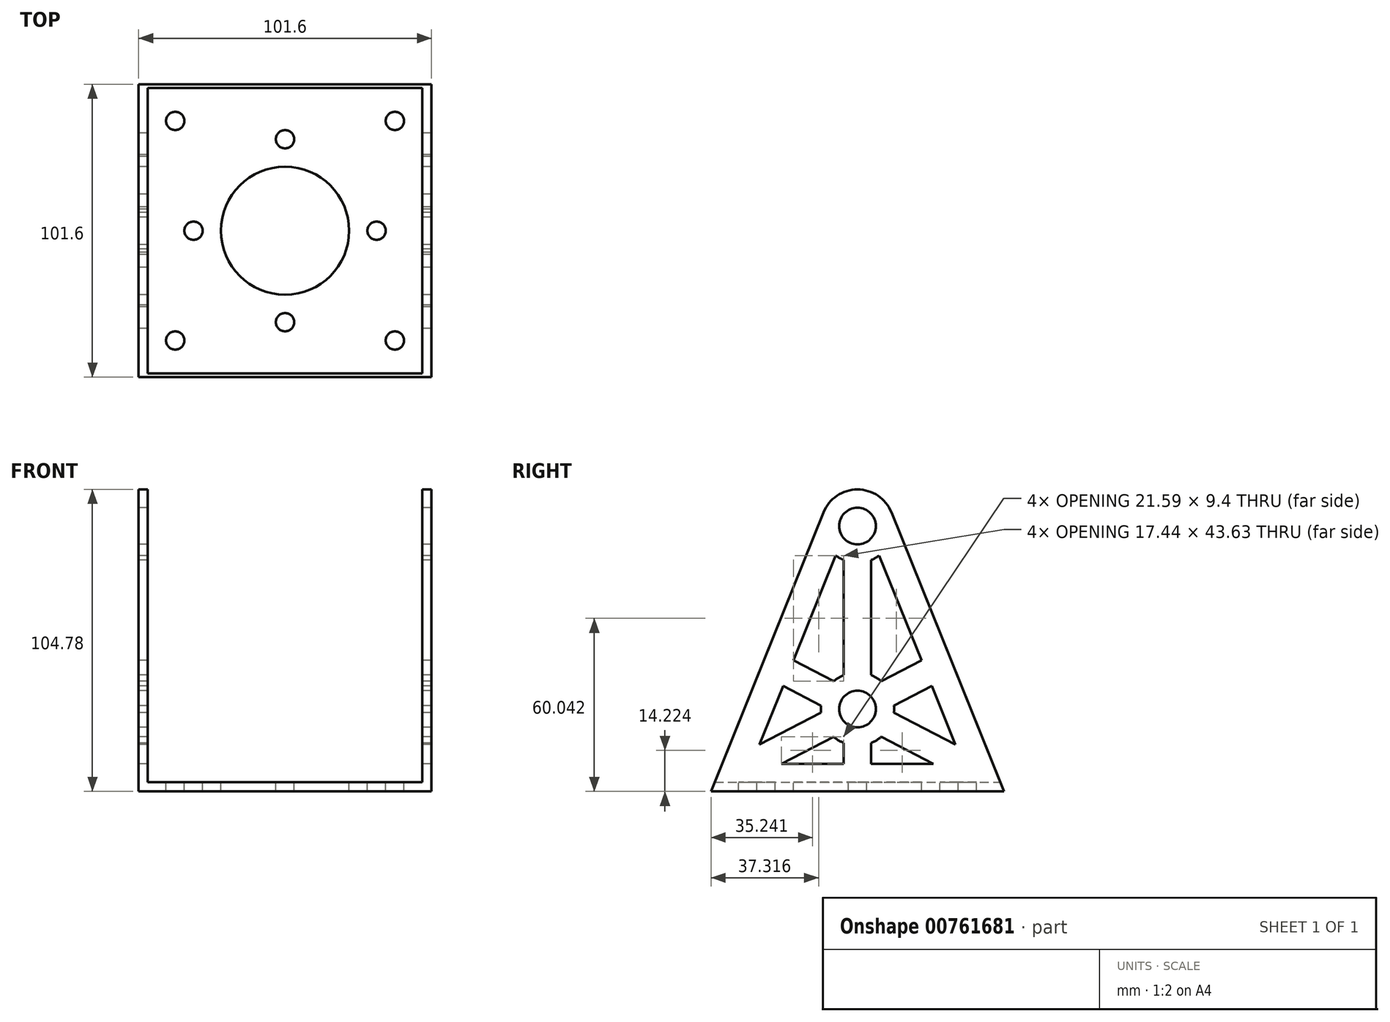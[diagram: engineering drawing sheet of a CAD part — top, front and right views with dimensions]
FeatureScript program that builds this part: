
annotation { "Feature Type Name" : "Feature", "Feature Type Description" : "" }
export const myFeature = defineFeature(function(context is Context, id is Id, definition is map)
    precondition{}
    {
        {
            var Q0;
            Q0=qCreatedBy(makeId("Top.planeOp"),FACE);
            var sketch = newSketch(context, id + "F0", { "sketchPlane" : qUnion([Q0])});
            skLineSegment(sketch, "E0.bottom", {"start": v(50.8, 50.8) * mm, "end": v(-50.8, 50.8) * mm});
            skLineSegment(sketch, "E0.top", {"start": v(50.8, -50.8) * mm, "end": v(-50.8, -50.8) * mm});
            skLineSegment(sketch, "E0.left", {"start": v(50.8, 50.8) * mm, "end": v(50.8, -50.8) * mm});
            skLineSegment(sketch, "E0.right", {"start": v(-50.8, 50.8) * mm, "end": v(-50.8, -50.8) * mm});
            skPoint(sketch, "E0.middle", {"position": v(0, 0) * mm});
            skSolve(sketch);
        }
        {
            var Q0;
            Q0 = qSketchRegion(id + "F0", true);
            extrude(context, id + "F1", {"entities" : qUnion([Q0]), "depth" : 3.17 * mm, "offsetDistance" : 25.4 * mm});
        }
        {
            var Q0;
            Q0=makeQuery(id+"F1.opExtrude","CAP_FACE",FACE,{"disambiguationData":[OSD([sQuery(id+"F0.wireOp",EDGE,"E0.bottom"),sQuery(id+"F0.wireOp",EDGE,"E0.top"),sQuery(id+"F0.wireOp",EDGE,"E0.left"),sQuery(id+"F0.wireOp",EDGE,"E0.right")])],"isStart":false});
            var sketch = newSketch(context, id + "F2", { "sketchPlane" : qUnion([Q0])});
            skLineSegment(sketch, "E1", {"start": v(-50.8, 50.8) * mm, "end": v(-50.8, -50.8) * mm});
            skLineSegment(sketch, "E2", {"start": v(-50.8, -50.8) * mm, "end": v(-47.62, -50.8) * mm});
            skLineSegment(sketch, "E3", {"start": v(-47.62, -50.8) * mm, "end": v(-47.63, 50.8) * mm});
            skLineSegment(sketch, "E4", {"start": v(-47.63, 50.8) * mm, "end": v(-50.8, 50.8) * mm});
            skSolve(sketch);
        }
        {
            var Q0;
            Q0=makeQuery(id+"F2.imprint","IMPRINT",FACE,{"disambiguationData":[TD([[makeQuery(id+"F2.imprint","IMPRINT",EDGE,{"derivedFrom":sQuery(id+"F2.wireOp",EDGE,"E1")}),1.0]])]});
            extrude(context, id + "F3", {"entities" : qUnion([Q0]), "operationType" : NewBodyOperationType.ADD, "depth" : 101.6 * mm, "offsetDistance" : 25.4 * mm});
        }
        {
            var Q0;
            Q0=makeQuery(id+"F1.opExtrude","CAP_FACE",FACE,{"disambiguationData":[OSD([sQuery(id+"F0.wireOp",EDGE,"E0.bottom"),sQuery(id+"F0.wireOp",EDGE,"E0.top"),sQuery(id+"F0.wireOp",EDGE,"E0.left"),sQuery(id+"F0.wireOp",EDGE,"E0.right")])],"isStart":false});
            var sketch = newSketch(context, id + "F4", { "sketchPlane" : qUnion([Q0])});
            skLineSegment(sketch, "E5.bottom", {"start": v(50.8, 50.8) * mm, "end": v(47.62, 50.8) * mm});
            skLineSegment(sketch, "E5.top", {"start": v(50.8, -50.8) * mm, "end": v(47.63, -50.8) * mm});
            skLineSegment(sketch, "E5.left", {"start": v(50.8, 50.8) * mm, "end": v(50.8, -50.8) * mm});
            skLineSegment(sketch, "E5.right", {"start": v(47.62, 50.8) * mm, "end": v(47.63, -50.8) * mm});
            skSolve(sketch);
        }
        {
            var Q0;
            Q0=makeQuery(id+"F4.imprint","IMPRINT",FACE,{"disambiguationData":[TD([[makeQuery(id+"F4.imprint","IMPRINT",EDGE,{"derivedFrom":sQuery(id+"F4.wireOp",EDGE,"E5.bottom")}),1.0]])]});
            extrude(context, id + "F5", {"entities" : qUnion([Q0]), "operationType" : NewBodyOperationType.ADD, "depth" : 101.6 * mm, "offsetDistance" : 25.4 * mm});
        }
        {
            var Q0;
            Q0=makeQuery(id+"F3.boolean.opBoolean","MERGE",FACE,{"derivedFrom":[makeQuery(id+"F1.opExtrude","SWEPT_FACE",FACE,{"disambiguationData":[OSD([sQuery(id+"F0.wireOp",EDGE,"E0.right")])]}),makeQuery(id+"F3.opExtrude","SWEPT_FACE",FACE,{"disambiguationData":[OSD([sQuery(id+"F2.wireOp",EDGE,"E1")])]})]});
            var sketch = newSketch(context, id + "F6", { "sketchPlane" : qUnion([Q0])});
            skLineSegment(sketch, "E6", {"start": v(-50.8, 0) * mm, "end": v(-11.78, 96.82) * mm});
            skLineSegment(sketch, "E7", {"start": v(50.8, 0) * mm, "end": v(11.78, 96.82) * mm});
            skArc(sketch, "E8", {"start": v(11.78, 96.82) * mm, "mid": v(0, 104.78) * mm, "end": v(-11.78, 96.82) * mm});
            skSolve(sketch);
        }
        {
            var Q0;
            Q0 = qSketchRegion(id + "F6", true);
            var Q1;
            {var subQ0=sQuery(id+"F6.wireOp",EDGE,"E6");Q1=makeQuery(id+"F6.imprint","IMPRINT",FACE,{"disambiguationData":[TD([[makeQuery(id+"F6.imprint","IMPRINT",EDGE,{"derivedFrom":subQ0}),1.0]])]});}
            var Q2;
            {var subQ0=sQuery(id+"F6.wireOp",EDGE,"E7");Q2=makeQuery(id+"F6.imprint","IMPRINT",FACE,{"disambiguationData":[TD([[makeQuery(id+"F6.imprint","IMPRINT",EDGE,{"derivedFrom":subQ0}),-1.0]])]});}
            extrude(context, id + "F7", {"entities" : qUnion([Q0, Q1, Q2]), "operationType" : NewBodyOperationType.REMOVE, "oppositeDirection" : true, "depth" : 101.6 * mm, "offsetDistance" : 25.4 * mm});
        }
        {
            var Q0;
            Q0=makeQuery(id+"F3.boolean.opBoolean","MERGE",FACE,{"derivedFrom":[makeQuery(id+"F1.opExtrude","SWEPT_FACE",FACE,{"disambiguationData":[OSD([sQuery(id+"F0.wireOp",EDGE,"E0.right")])]}),makeQuery(id+"F3.opExtrude","SWEPT_FACE",FACE,{"disambiguationData":[OSD([sQuery(id+"F2.wireOp",EDGE,"E1")])]})]});
            var sketch = newSketch(context, id + "F8", { "sketchPlane" : qUnion([Q0])});
            skCircle(sketch, "E9", {"center": v(0, 92.08) * mm, "radius": 6.35 * mm});
            skCircle(sketch, "E10", {"center": v(0, 28.58) * mm, "radius": 6.35 * mm});
            skSolve(sketch);
        }
        {
            var Q0;
            Q0=makeQuery(id+"F8.imprint","IMPRINT",FACE,{"disambiguationData":[TD([[makeQuery(id+"F8.imprint","IMPRINT",EDGE,{"derivedFrom":sQuery(id+"F8.wireOp",EDGE,"E10")}),1.0]])]});
            var Q1;
            Q1=makeQuery(id+"F8.imprint","IMPRINT",FACE,{"disambiguationData":[TD([[makeQuery(id+"F8.imprint","IMPRINT",EDGE,{"derivedFrom":sQuery(id+"F8.wireOp",EDGE,"E9")}),1.0]])]});
            extrude(context, id + "F9", {"entities" : qUnion([Q0, Q1]), "operationType" : NewBodyOperationType.REMOVE, "oppositeDirection" : true, "depth" : 101.6 * mm, "offsetDistance" : 25.4 * mm});
        }
        {
            var Q0;
            Q0=makeQuery(id+"F3.boolean.opBoolean","MERGE",FACE,{"derivedFrom":[makeQuery(id+"F1.opExtrude","SWEPT_FACE",FACE,{"disambiguationData":[OSD([sQuery(id+"F0.wireOp",EDGE,"E0.right")])]}),makeQuery(id+"F3.opExtrude","SWEPT_FACE",FACE,{"disambiguationData":[OSD([sQuery(id+"F2.wireOp",EDGE,"E1")])]})]});
            var sketch = newSketch(context, id + "F10", { "sketchPlane" : qUnion([Q0])});
            skCircle(sketch, "E11", {"center": v(0, 28.58) * mm, "radius": 12.7 * mm});
            skLineSegment(sketch, "E12", {"start": v(-4.76, 80.3) * mm, "end": v(-4.76, 9.53) * mm});
            skLineSegment(sketch, "E13", {"start": v(4.76, 80.3) * mm, "end": v(4.76, 9.53) * mm});
            skLineSegment(sketch, "E14", {"start": v(4.76, 9.53) * mm, "end": v(36.7, 9.53) * mm});
            skLineSegment(sketch, "E15", {"start": v(36.7, 9.52) * mm, "end": v(7.54, 81.86) * mm});
            skCircle(sketch, "E16", {"center": v(0, 92.08) * mm, "radius": 12.7 * mm});
            skLineSegment(sketch, "E17", {"start": v(-4.76, 9.53) * mm, "end": v(-36.7, 9.52) * mm});
            skLineSegment(sketch, "E18", {"start": v(-36.7, 9.52) * mm, "end": v(-7.54, 81.86) * mm});
            skLineSegment(sketch, "E19", {"start": v(36.7, 9.53) * mm, "end": v(-24, 41.03) * mm, "construction": true});
            skLineSegment(sketch, "E20", {"start": v(24, 41.03) * mm, "end": v(-36.7, 9.52) * mm, "construction": true});
            skLineSegment(sketch, "E21", {"start": v(-33.96, 16.31) * mm, "end": v(-12.64, 27.38) * mm});
            skLineSegment(sketch, "E22", {"start": v(-26.36, 9.52) * mm, "end": v(-8.25, 18.92) * mm});
            skLineSegment(sketch, "E23.trimOffspring", {"start": v(8.25, 38.23) * mm, "end": v(22.2, 45.47) * mm});
            skLineSegment(sketch, "E24.trimOffspring", {"start": v(12.64, 29.77) * mm, "end": v(25.78, 36.6) * mm});
            skLineSegment(sketch, "E25", {"start": v(-22.2, 45.47) * mm, "end": v(-8.25, 38.23) * mm});
            skLineSegment(sketch, "E26", {"start": v(8.25, 18.92) * mm, "end": v(26.36, 9.52) * mm});
            skLineSegment(sketch, "E27.trimOffspring", {"start": v(-25.78, 36.6) * mm, "end": v(-12.64, 29.77) * mm});
            skLineSegment(sketch, "E28.trimOffspring", {"start": v(12.64, 27.38) * mm, "end": v(33.96, 16.31) * mm});
            skSolve(sketch);
        }
        {
            var Q0;
            {var subQ6=sQuery(id+"F10.wireOp",EDGE,"E23.trimOffspring");Q0=makeQuery(id+"F10.imprint","IMPRINT",FACE,{"disambiguationData":[TD([[makeQuery(id+"F10.imprint","IMPRINT",EDGE,{"derivedFrom":subQ6}),1.0]])]});}
            var Q1;
            {var subQ0=sQuery(id+"F10.wireOp",EDGE,"E24.trimOffspring");Q1=makeQuery(id+"F10.imprint","IMPRINT",FACE,{"disambiguationData":[TD([[makeQuery(id+"F10.imprint","IMPRINT",EDGE,{"derivedFrom":subQ0}),-1.0]])]});}
            var Q2;
            {var subQ0=sQuery(id+"F10.wireOp",EDGE,"E13");Q2=makeQuery(id+"F10.imprint","IMPRINT",FACE,{"disambiguationData":[TD([[makeQuery(id+"F10.imprint","IMPRINT",EDGE,{"derivedFrom":subQ0}),1.0]])]});}
            var Q3;
            {var subQ0=sQuery(id+"F10.wireOp",EDGE,"E12");Q3=makeQuery(id+"F10.imprint","IMPRINT",FACE,{"disambiguationData":[TD([[makeQuery(id+"F10.imprint","IMPRINT",EDGE,{"derivedFrom":subQ0}),-1.0]])]});}
            var Q4;
            {var subQ0=sQuery(id+"F10.wireOp",EDGE,"E21");Q4=makeQuery(id+"F10.imprint","IMPRINT",FACE,{"disambiguationData":[TD([[makeQuery(id+"F10.imprint","IMPRINT",EDGE,{"derivedFrom":subQ0}),1.0]])]});}
            var Q5;
            {var subQ0=sQuery(id+"F10.wireOp",EDGE,"E22");Q5=makeQuery(id+"F10.imprint","IMPRINT",FACE,{"disambiguationData":[TD([[makeQuery(id+"F10.imprint","IMPRINT",EDGE,{"derivedFrom":subQ0}),-1.0]])]});}
            var Q6;
            {var subQ0=sQuery(id+"F10.wireOp",EDGE,"E26");Q6=makeQuery(id+"F10.imprint","IMPRINT",FACE,{"disambiguationData":[TD([[makeQuery(id+"F10.imprint","IMPRINT",EDGE,{"derivedFrom":subQ0}),-1.0]])]});}
            var Q7;
            {var subQ3=sQuery(id+"F10.wireOp",EDGE,"E25");Q7=makeQuery(id+"F10.imprint","IMPRINT",FACE,{"disambiguationData":[TD([[makeQuery(id+"F10.imprint","IMPRINT",EDGE,{"derivedFrom":subQ3}),1.0]])]});}
            extrude(context, id + "F11", {"entities" : qUnion([Q0, Q1, Q2, Q3, Q4, Q5, Q6, Q7]), "operationType" : NewBodyOperationType.REMOVE, "oppositeDirection" : true, "depth" : 101.6 * mm, "offsetDistance" : 25.4 * mm});
        }
        {
            var Q0;
            Q0=makeQuery(id+"F1.opExtrude","CAP_FACE",FACE,{"disambiguationData":[OSD([sQuery(id+"F0.wireOp",EDGE,"E0.bottom"),sQuery(id+"F0.wireOp",EDGE,"E0.top"),sQuery(id+"F0.wireOp",EDGE,"E0.left"),sQuery(id+"F0.wireOp",EDGE,"E0.right")])],"isStart":false});
            var sketch = newSketch(context, id + "F12", { "sketchPlane" : qUnion([Q0])});
            skCircle(sketch, "E29", {"center": v(0, 0) * mm, "radius": 22.23 * mm});
            skCircle(sketch, "E30", {"center": v(-38.1, 38.1) * mm, "radius": 3.18 * mm});
            skCircle(sketch, "E31", {"center": v(38.1, 38.1) * mm, "radius": 3.18 * mm});
            skCircle(sketch, "E32", {"center": v(38.1, -38.1) * mm, "radius": 3.17 * mm});
            skCircle(sketch, "E33", {"center": v(-38.1, -38.1) * mm, "radius": 3.18 * mm});
            skLineSegment(sketch, "E34.bottom", {"start": v(38.1, -38.1) * mm, "end": v(-38.1, -38.1) * mm, "construction": true});
            skLineSegment(sketch, "E34.top", {"start": v(38.1, 38.1) * mm, "end": v(-38.1, 38.1) * mm, "construction": true});
            skLineSegment(sketch, "E34.left", {"start": v(38.1, -38.1) * mm, "end": v(38.1, 38.1) * mm, "construction": true});
            skLineSegment(sketch, "E34.right", {"start": v(-38.1, -38.1) * mm, "end": v(-38.1, 38.1) * mm, "construction": true});
            skCircle(sketch, "E35", {"center": v(0, 0) * mm, "radius": 31.75 * mm, "construction": true});
            skCircle(sketch, "E36", {"center": v(-31.75, 0) * mm, "radius": 3.18 * mm});
            skCircle(sketch, "E37", {"center": v(0, 31.75) * mm, "radius": 3.18 * mm});
            skPoint(sketch, "E37.centerSnap0", {"position": v(0, 38.1) * mm});
            skCircle(sketch, "E38", {"center": v(31.75, 0) * mm, "radius": 3.18 * mm});
            skCircle(sketch, "E39", {"center": v(0, -31.75) * mm, "radius": 3.18 * mm});
            skPoint(sketch, "E39.centerSnap0", {"position": v(0, -38.1) * mm});
            skSolve(sketch);
        }
        {
            var Q0;
            Q0=makeQuery(id+"F12.imprint","IMPRINT",FACE,{"disambiguationData":[TD([[makeQuery(id+"F12.imprint","IMPRINT",EDGE,{"derivedFrom":sQuery(id+"F12.wireOp",EDGE,"E31")}),1.0]])]});
            var Q1;
            Q1=makeQuery(id+"F12.imprint","IMPRINT",FACE,{"disambiguationData":[TD([[makeQuery(id+"F12.imprint","IMPRINT",EDGE,{"derivedFrom":sQuery(id+"F12.wireOp",EDGE,"E38")}),1.0]])]});
            var Q2;
            Q2=makeQuery(id+"F12.imprint","IMPRINT",FACE,{"disambiguationData":[TD([[makeQuery(id+"F12.imprint","IMPRINT",EDGE,{"derivedFrom":sQuery(id+"F12.wireOp",EDGE,"E32")}),1.0]])]});
            var Q3;
            Q3=makeQuery(id+"F12.imprint","IMPRINT",FACE,{"disambiguationData":[TD([[makeQuery(id+"F12.imprint","IMPRINT",EDGE,{"derivedFrom":sQuery(id+"F12.wireOp",EDGE,"E29")}),1.0]])]});
            var Q4;
            Q4=makeQuery(id+"F12.imprint","IMPRINT",FACE,{"disambiguationData":[TD([[makeQuery(id+"F12.imprint","IMPRINT",EDGE,{"derivedFrom":sQuery(id+"F12.wireOp",EDGE,"E39")}),1.0]])]});
            var Q5;
            Q5=makeQuery(id+"F12.imprint","IMPRINT",FACE,{"disambiguationData":[TD([[makeQuery(id+"F12.imprint","IMPRINT",EDGE,{"derivedFrom":sQuery(id+"F12.wireOp",EDGE,"E36")}),1.0]])]});
            var Q6;
            Q6=makeQuery(id+"F12.imprint","IMPRINT",FACE,{"disambiguationData":[TD([[makeQuery(id+"F12.imprint","IMPRINT",EDGE,{"derivedFrom":sQuery(id+"F12.wireOp",EDGE,"E37")}),1.0]])]});
            var Q7;
            Q7=makeQuery(id+"F12.imprint","IMPRINT",FACE,{"disambiguationData":[TD([[makeQuery(id+"F12.imprint","IMPRINT",EDGE,{"derivedFrom":sQuery(id+"F12.wireOp",EDGE,"E30")}),1.0]])]});
            var Q8;
            Q8=makeQuery(id+"F12.imprint","IMPRINT",FACE,{"disambiguationData":[TD([[makeQuery(id+"F12.imprint","IMPRINT",EDGE,{"derivedFrom":sQuery(id+"F12.wireOp",EDGE,"E33")}),1.0]])]});
            extrude(context, id + "F13", {"entities" : qUnion([Q0, Q1, Q2, Q3, Q4, Q5, Q6, Q7, Q8]), "operationType" : NewBodyOperationType.REMOVE, "oppositeDirection" : true, "depth" : 25.4 * mm, "offsetDistance" : 25.4 * mm});
        }
    });
